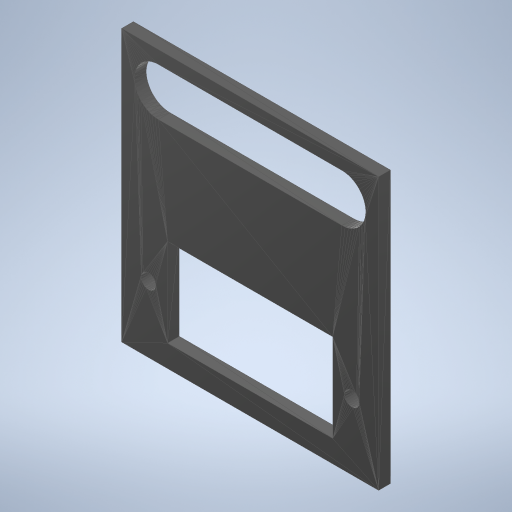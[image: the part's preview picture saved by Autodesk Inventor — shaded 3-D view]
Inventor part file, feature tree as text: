
AUTODESK INVENTOR PART (.ipt)
format: ipt  version: 2023 (Build 270158000, 158)  size: 252,928 bytes
history: native  units: in
note: dims shown in document units (in); Inventor stores cm internally (conversion verified against a paired STEP export)
features: other x2, plane x1
ambient origin geometry x8: Origin, YZ Plane, XZ Plane, XY Plane, X Axis, Y Axis, Z Axis, Center Point
feature tree (3):
  other  "Servo_mount_flat"
  plane  "Work Plane1"
  other  "MeshFeature1"
